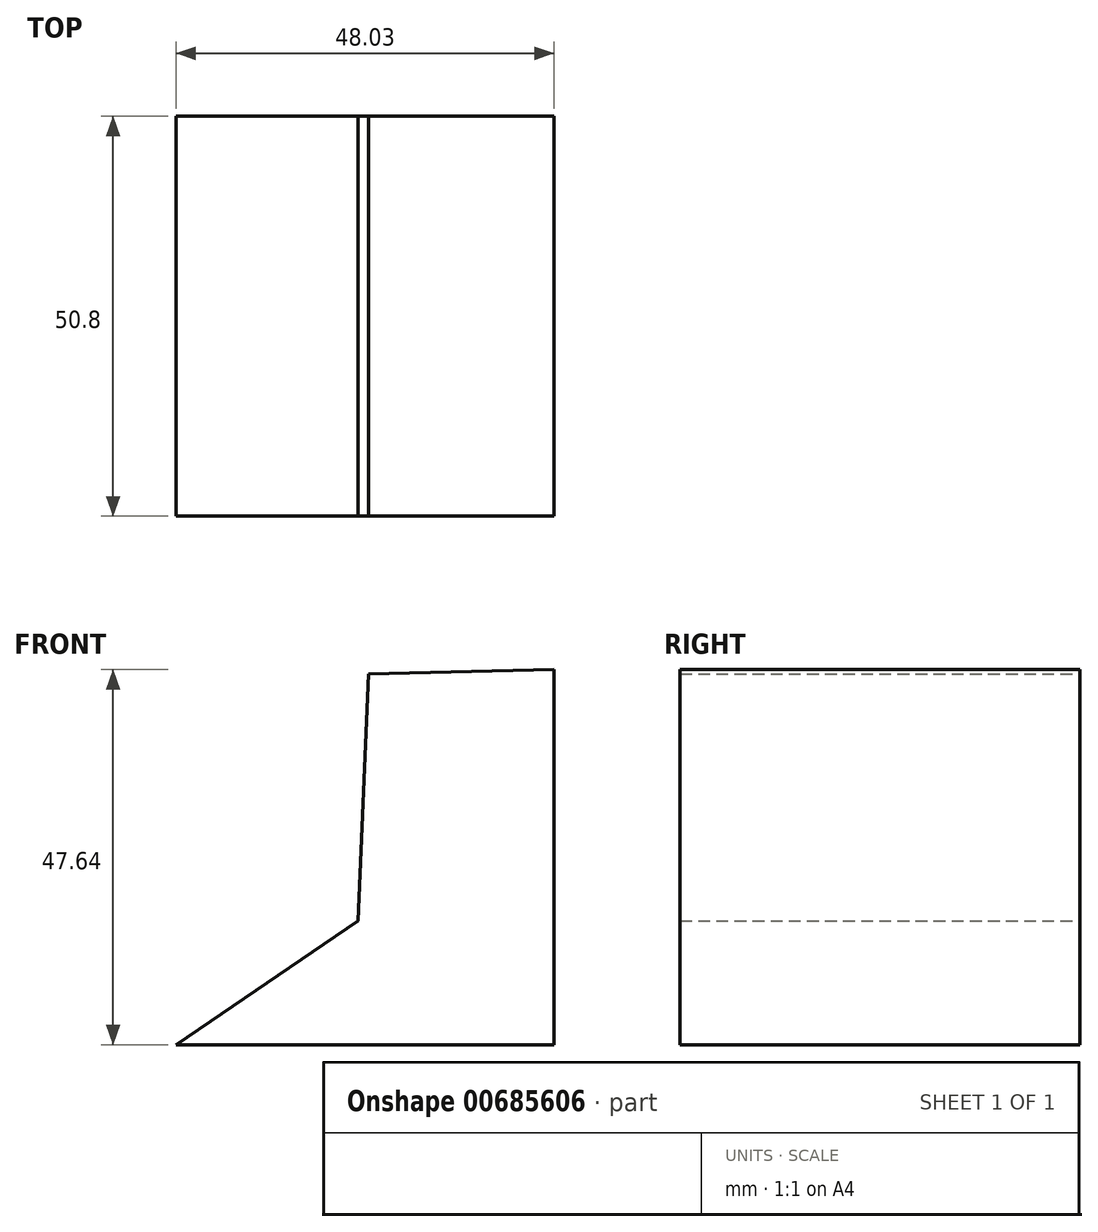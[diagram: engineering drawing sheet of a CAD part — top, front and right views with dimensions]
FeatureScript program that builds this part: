
annotation { "Feature Type Name" : "Feature", "Feature Type Description" : "" }
export const myFeature = defineFeature(function(context is Context, id is Id, definition is map)
    precondition{}
    {
        {
            var Q0;
            Q0=qCreatedBy(makeId("Front.planeOp"),FACE);
            var sketch = newSketch(context, id + "F0", { "sketchPlane" : qUnion([Q0])});
            skLineSegment(sketch, "E0", {"start": v(0, 47.64) * mm, "end": v(0, 0) * mm});
            skLineSegment(sketch, "E1", {"start": v(0, 0) * mm, "end": v(-48.03, 0) * mm});
            skLineSegment(sketch, "E2", {"start": v(-48.03, 0) * mm, "end": v(-24.92, 15.75) * mm});
            skLineSegment(sketch, "E3", {"start": v(-24.92, 15.75) * mm, "end": v(-23.58, 47.07) * mm});
            skLineSegment(sketch, "E4", {"start": v(-23.58, 47.07) * mm, "end": v(0, 47.64) * mm});
            skSolve(sketch);
        }
        {
            var Q0;
            Q0 = qSketchRegion(id + "F0", true);
            extrude(context, id + "F1", {"entities" : qUnion([Q0]), "depth" : 50.8 * mm, "offsetDistance" : 25.4 * mm});
        }
    });
